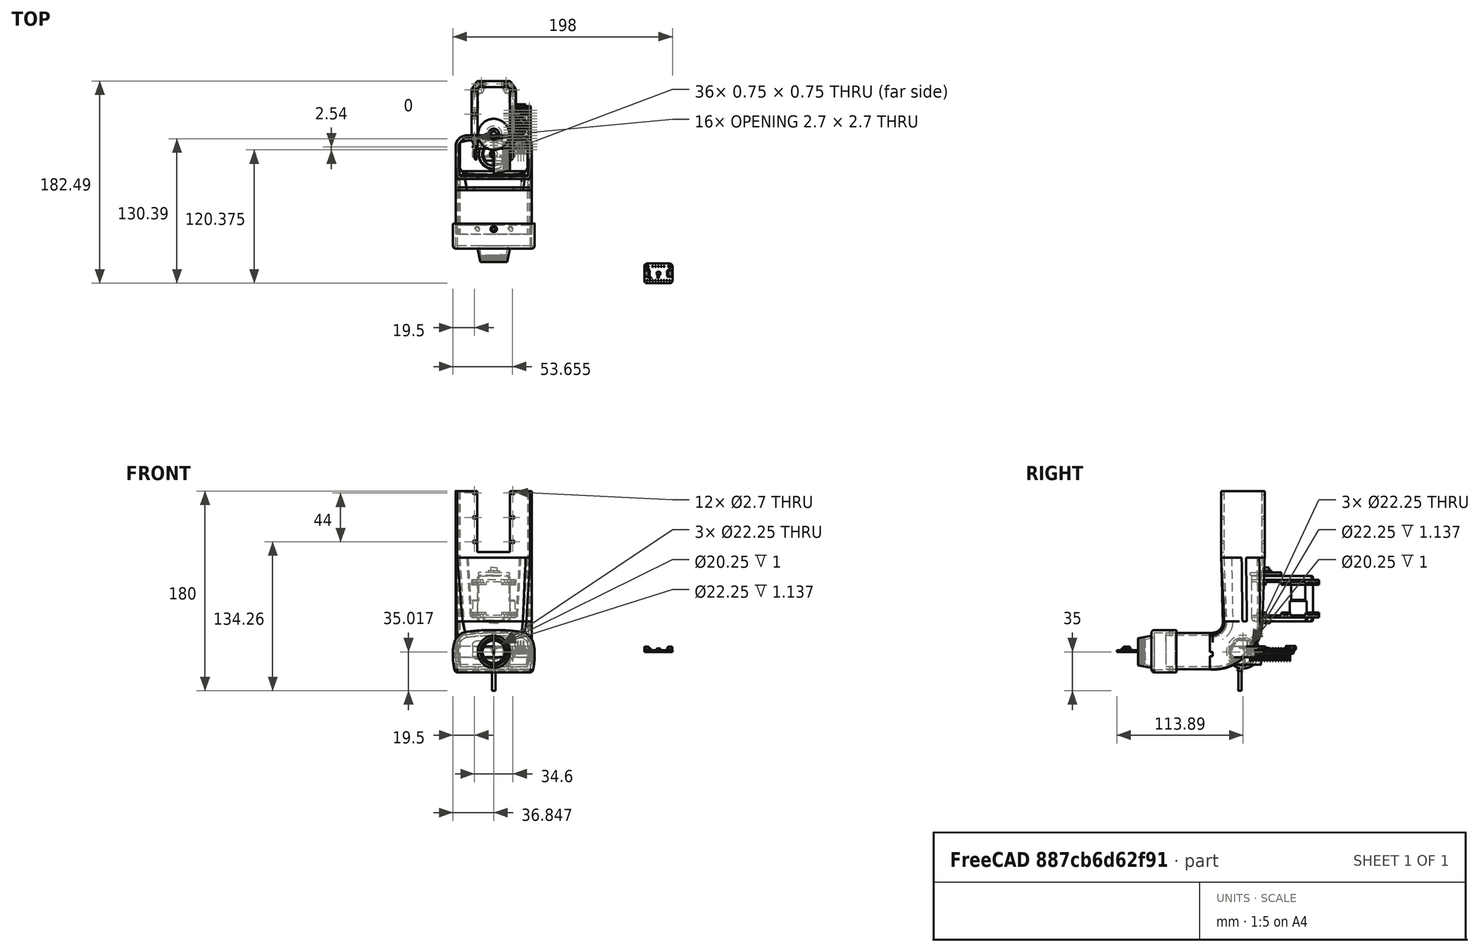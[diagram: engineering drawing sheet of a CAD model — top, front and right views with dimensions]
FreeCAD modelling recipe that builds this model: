
FCSTD DOCUMENT  (FreeCAD 0.20R29177 +426 (Git))
Label: new-mapping-unit 
License: All rights reserved
LicenseURL: http://en.wikipedia.org/wiki/All_rights_reserved
objects: Part::Feature×37, Sketcher::SketchObject×15, PartDesign::Hole×5, PartDesign::Pocket×3, PartDesign::Body×3, App::LinkGroup×2, Spreadsheet::Sheet×2, Part::Compound2×2, Part::Part2DObjectPython×2, PartDesign::AdditiveLoft×2, Mesh::Feature×1, PartDesign::Revolution×1, PartDesign::Pad×1, PartDesign::Thickness×1, PartDesign::SubtractivePipe×1, PartDesign::SubtractiveHelix×1, PartDesign::Boolean×1, PartDesign::AdditivePipe×1
note: 90 computed .brp shape members not serialized (recipe doc carries the construction recipe); baked Part::Feature solids carry a one-line shape summary decoded from their .brp

FEATURE [Part::Feature] Solid  label="DC05_M01_DUMMY"
  Placement = pos=(0,20.5,48) rot=(0,0,1;3.14159rad)
  shape: bbox 40.22 x 62.12 x 50.02 mm, 366 faces (baked)
FEATURE [Mesh::Feature] lidar_mounting_bracket_Body  label="lidar-mounting-bracket-Body"
  Placement = pos=(-0.23,-44.82,76.58) rot=(0.57735,0.57735,0.57735;4.18879rad)
FEATURE [App::LinkGroup] LinkGroup  label="servoLidar"
  ElementList = -> [Solid,lidar_mounting_bracket_Body]
  LinkMode = 0
  Placement = pos=(5.96046e-08,48,82.76) rot=(1,0,0;1.5708rad)
FEATURE [Sketcher::SketchObject] Sketch008
  FullyConstrained = false
  MapMode = 5
  Support = -> [XY_Plane002]
  expr: Constraints[9] = 22.25mm / 2
  sketch-geometry (8):
    g0: LineSegment StartX=9.7 StartY=11.125 StartZ=0 EndX=13.7 EndY=11.125 EndZ=0
    g1: LineSegment StartX=13.7 StartY=11.125 StartZ=0 EndX=13.7 EndY=10.125 EndZ=0
    g2: LineSegment StartX=13.7 StartY=10.125 StartZ=0 EndX=14.7 EndY=10.125 EndZ=0
    g3: LineSegment StartX=14.7 StartY=10.125 StartZ=0 EndX=14.7 EndY=12.1585 EndZ=0
    g4: LineSegment StartX=14.7 StartY=12.1585 StartZ=0 EndX=0 EndY=15 EndZ=0
    g5: LineSegment StartX=0 StartY=15 StartZ=0 EndX=0 EndY=13 EndZ=0
    g6: LineSegment StartX=9.7 StartY=11.125 StartZ=0 EndX=0 EndY=13 EndZ=0
    g7: GeomPoint X=4.20241 Y=12.8749 Z=0
  constraints (21):
    c: Horizontal(g0)
    c: Coincident(g0,g1)
    c: Vertical(g1)
    c: Coincident(g1,g2)
    c: Horizontal(g2)
    c: Coincident(g2,g3)
    c: Vertical(g3)
    c: Coincident(g3,g4)
    c: PointOnObject(g4,g-2)
    c: DistanceY(g-1,g0) = 11.125
    c: DistanceY(g1,g1) = 1
    c: DistanceX(g2,g2) = 1
    c: DistanceX(g0,g0) = 4
    c: DistanceX(g-1,g0) = 13.7
    c: PointOnObject(g5,g-2)
    c: Coincident(g5,g4)
    c: DistanceY(g-1,g4) = 15
    c: Coincident(g6,g0)
    c: Coincident(g6,g5)
    c: Parallel(g6,g4)
    c: DistanceY(g5,g5) = 2
FEATURE [PartDesign::Revolution] Revolution
  Angle = 360
  Axis = (1,0,0)
  Base = (0,0,0)
  Profile = -> Sketch008
  ReferenceAxis = -> Sketch008 [H_Axis]
FEATURE [Sketcher::SketchObject] Sketch009  label="baseSketch"
  FullyConstrained = true
  MapMode = 5
  Placement = pos=(0,0,0) rot=(0.57735,0.57735,0.57735;2.0944rad)
  Support = -> [YZ_Plane003]
  expr: Constraints[14] = <<params>>.cameraWidthBottom
  expr: Constraints[17] = <<params>>.notchWidth
  expr: Constraints[29] = <<params>>.cameraWidth
  expr: Constraints[7] = <<params>>.cameraHeight
  sketch-geometry (12):
    g0: LineSegment StartX=32.85 StartY=-16 StartZ=0 EndX=-32.85 EndY=-16 EndZ=0
    g1: ArcOfCircle CenterX=-22.9627 CenterY=5.1188 CenterZ=0 NormalX=0 NormalY=0 NormalZ=1 AngleXU=0 Radius=10.5 StartAngle=1.72137 EndAngle=2.7983
    g2: ArcOfCircle CenterX=22.9627 CenterY=5.1188 CenterZ=0 NormalX=0 NormalY=0 NormalZ=1 AngleXU=0 Radius=10.5 StartAngle=0.34329 EndAngle=1.42022
    g3: ArcOfCircle CenterX=-2 CenterY=-133.046 CenterZ=0 NormalX=0 NormalY=0 NormalZ=1 AngleXU=0 Radius=150.246 StartAngle=1.5708 EndAngle=1.72137
    g4: ArcOfCircle CenterX=2 CenterY=-133.046 CenterZ=0 NormalX=0 NormalY=0 NormalZ=1 AngleXU=0 Radius=150.246 StartAngle=1.42022 EndAngle=1.5708
    g5: LineSegment StartX=-2 StartY=17.2 StartZ=0 EndX=2 EndY=17.2 EndZ=0
    g6: ArcOfCircle CenterX=-8.64204 CenterY=0 CenterZ=0 NormalX=0 NormalY=0 NormalZ=1 AngleXU=0 Radius=25.708 StartAngle=2.7983 EndAngle=3.14159
    g7: ArcOfCircle CenterX=14.4 CenterY=-4 CenterZ=0 NormalX=0 NormalY=0 NormalZ=1 AngleXU=0 Radius=48.75 StartAngle=3.14159 EndAngle=3.3903
    g8: LineSegment StartX=-34.35 StartY=3.1e-15 StartZ=0 EndX=-34.35 EndY=-4 EndZ=0
    g9: ArcOfCircle CenterX=-14.4 CenterY=-4 CenterZ=0 NormalX=0 NormalY=0 NormalZ=1 AngleXU=0 Radius=48.75 StartAngle=6.03448 EndAngle=6.28319
    g10: ArcOfCircle CenterX=8.64204 CenterY=-9.8e-15 CenterZ=0 NormalX=0 NormalY=0 NormalZ=1 AngleXU=0 Radius=25.708 StartAngle=0 EndAngle=0.34329
    g11: LineSegment StartX=34.35 StartY=-9.8e-15 StartZ=0 EndX=34.35 EndY=-4 EndZ=0
  constraints (32):
    c: Distance(g-1,g0) = 16
    c: Equal(g2,g1)
    c: Symmetric(g0,g0,g-2)
    c: Diameter(g1) = 21
    c: Equal(g4,g3)
    c: Tangent(g4,g2) = -1.5708
    c: Tangent(g3,g1) = -1.5708
    c: Distance(g3,g0) = 33.2
    c: Coincident(g7,g0)
    c: Tangent(g6,g1) = -1.5708
    c: Coincident(g9,g0)
    c: Tangent(g10,g2) = -1.5708
    c: Symmetric(g2,g1,g-2)
    c: Vertical(g1,g0)
    c: DistanceX(g0,g0) = 65.7
    c: Distance(g2,g0) = 31.5
    c: Horizontal(g5)
    c: DistanceX(g5,g5) = 4
    c: Tangent(g5,g4) = 1.5708
    c: Tangent(g5,g3) = 1.5708
    c: Vertical(g8)
    c: Vertical(g11)
    c: Equal(g8,g11)
    c: Equal(g11,g5)
    c: Tangent(g8,g7) = -1.5708
    c: Tangent(g8,g6) = -1.5708
    c: Tangent(g11,g9) = 1.5708
    c: Tangent(g11,g10) = 1.5708
    c: Equal(g9,g7)
    c: DistanceX(g6,g10) = 68.7
    c: PointOnObject(g6,g-1)
    c: Equal(g6,g10)
FEATURE [PartDesign::Pad] Pad003  label="Pad"
  Direction = (1,-2e-16,3e-16)
  Length = 20
  Length2 = 10
  Placement = pos=(0,0,0) rot=(0.57735,0.57735,0.57735;2.0944rad)
  Profile = -> Sketch009
  ReferenceAxis = -> Sketch009 [N_Axis]
  Reversed = true
  Type = 0
  expr: Length = <<params>>.cameraDepth
FEATURE [PartDesign::Thickness] Thickness
  Base = -> Pad003 [Face14]
  BaseFeature = -> Pad003
  Intersection = false
  Join = 0
  Mode = 0
  SupportTransform = false
  Value = 2.5
  expr: Value = <<params>>.wallThickness
FEATURE [Sketcher::SketchObject] Sketch010  label="Sketch002"
  FullyConstrained = true
  MapMode = 5
  Placement = pos=(0,0,0) rot=(0.57735,0.57735,0.57735;2.0944rad)
  Support = -> [YZ_Plane003]
  sketch-geometry (1):
    g0: Circle CenterX=0 CenterY=0 CenterZ=0 NormalX=0 NormalY=0 NormalZ=1 AngleXU=0 Radius=13
  constraints (2):
    c: Coincident(g0,g-1)
    c: Diameter(g0) = 26
FEATURE [PartDesign::Pocket] Pocket004  label="Pocket"
  BaseFeature = -> Thickness
  Direction = (-1,2e-16,-3e-16)
  Length = 5
  Length2 = 5
  Profile = -> Sketch010
  ReferenceAxis = -> Sketch010 [N_Axis]
  Reversed = true
  Type = 1
FEATURE [Spreadsheet::Sheet] Spreadsheet001  label="params"
  cells = A1=cameraWidth; B1(cameraWidth)==68.7mm; D1=wallThickness; E1(wallThickness)==2.5mm; A2=cameraWidthBottom; B2(cameraWidthBottom)==65.7mm; A3=cameraHeight; B3(cameraHeight)==33.2mm; A4=cameraDepth; B4(cameraDepth)==20mm; A5=cameraBottomToSensor; B5(cameraBottomToSensor)==16mm; A7=notchWidth; B7(notchWidth)==4mm
FEATURE [Sketcher::SketchObject] Sketch011  label="grooveSketch"
  FullyConstrained = true
  MapMode = 5
  Placement = pos=(0,0,0) rot=(1,0,0;1.5708rad)
  Support = -> [XZ_Plane003]
  expr: Constraints[6] = <<params>>.wallThickness / 2
  expr: Constraints[7] = <<params>>.cameraBottomToSensor
  expr: Constraints[8] = <<params>>.cameraDepth
  sketch-geometry (3):
    g0: LineSegment StartX=-20 StartY=-17.25 StartZ=0 EndX=-20 EndY=-16 EndZ=0
    g1: LineSegment StartX=-20 StartY=-17.25 StartZ=0 EndX=-18.75 EndY=-16 EndZ=0
    g2: LineSegment StartX=-18.75 StartY=-16 StartZ=0 EndX=-20 EndY=-16 EndZ=0
  constraints (9):
    c: Vertical(g0)
    c: Coincident(g0,g1)
    c: Coincident(g1,g2)
    c: Coincident(g2,g0)
    c: Horizontal(g2)
    c: Equal(g2,g0)
    c: DistanceX(g2,g2) = 1.25
    c: DistanceY(g0,g-1) = 16
    c: DistanceX(g0,g-1) = 20
FEATURE [PartDesign::SubtractivePipe] SubtractivePipe
  AuxilleryCurvelinear = true
  AuxillerySpineTangent = false
  BaseFeature = -> Pocket004
  Binormal = (0,0,0)
  Mode = 0
  Profile = -> Sketch011
  Spine = -> Pocket004 [Edge4,Edge10,Edge21,Edge22,Edge23,Edge24,Edge25,Edge26,Edge27,Edge28,Edge29,Edge7]
  SpineTangent = false
  Transformation = 0
  Transition = 1
FEATURE [Sketcher::SketchObject] Sketch014  label="Sketch006"
  FullyConstrained = true
  MapMode = 5
  Support = -> [XY_Plane002]
  expr: Constraints[7] = 22.25mm / 2 - 0.02mm
  sketch-geometry (3):
    g0: LineSegment StartX=12.951 StartY=-11.105 StartZ=0 EndX=13.3255 EndY=-11.7537 EndZ=0
    g1: LineSegment StartX=13.3255 StartY=-11.7537 StartZ=0 EndX=13.7 EndY=-11.105 EndZ=0
    g2: LineSegment StartX=13.7 StartY=-11.105 StartZ=0 EndX=12.951 EndY=-11.105 EndZ=0
  constraints (9):
    c: Coincident(g0,g1)
    c: Coincident(g1,g2)
    c: Coincident(g2,g0)
    c: Horizontal(g2)
    c: Equal(g1,g2)
    c: Equal(g2,g0)
    c: DistanceX(g2,g2) = 0.749
    c: DistanceY(g1,g-1) = 11.105
    c: DistanceX(g-1,g1) = 13.7
FEATURE [PartDesign::SubtractiveHelix] SubtractiveHelix
  Angle = 0
  Axis = (1,0,0)
  Base = (0,0,0)
  BaseFeature = -> Revolution
  Growth = 0
  HasBeenEdited = true
  Height = 5
  LeftHanded = false
  Mode = 0
  Outside = false
  Pitch = 0.75
  Profile = -> Sketch014
  ReferenceAxis = -> Sketch014 [H_Axis]
  Reversed = true
  Turns = 6.66667
FEATURE [PartDesign::Body] Body002  label="lense"
  Group = -> [Sketch008,Revolution,Sketch014,SubtractiveHelix]
  Origin = -> Origin002
  Tip = -> SubtractiveHelix
FEATURE [PartDesign::Boolean] Boolean002
  BaseFeature = -> SubtractivePipe
  Group = -> [Body002]
  Type = 0
FEATURE [Part::Feature] Feature  label="arduino nano001"
  Placement = pos=(32.0955,6.48515,2e-15) rot=(0.57735,0.57735,0.57735;2.0944rad)
  shape: bbox 18 x 45 x 18.6 mm, 6295 faces, 55 solids (baked)
FEATURE [Part::Feature] Solid002
  shape: bbox 68.8 x 33.82 x 71.73 mm, 134 faces (baked)
FEATURE [Part::Compound2] Compound  label="camera"
  Links = -> [Solid002]
  Placement = pos=(0,-74.85,-2.65) rot=(-1,0,0;4.71239rad)
FEATURE [Part::Feature] Solid003
  shape: bbox 2 x 1.25 x 1.25 mm, 28 faces (baked)
FEATURE [Part::Feature] Solid004
  shape: bbox 1.25 x 2 x 1.25 mm, 28 faces (baked)
FEATURE [Part::Feature] Solid005
  shape: bbox 1.5 x 0.2 x 1.25 mm, 25 faces (baked)
FEATURE [Part::Feature] Solid006
  shape: bbox 3.7 x 0.2 x 2.46 mm, 20 faces (baked)
FEATURE [Part::Feature] Solid007
  shape: bbox 3.7 x 0.2 x 2.46 mm, 20 faces (baked)
FEATURE [Part::Feature] Solid008
  shape: bbox 3.7 x 0.2 x 2.46 mm, 20 faces (baked)
FEATURE [Part::Feature] Solid009
  shape: bbox 1.5 x 0.2 x 1.25 mm, 25 faces (baked)
FEATURE [Part::Feature] Solid010
  shape: bbox 3.7 x 0.2 x 2.46 mm, 20 faces (baked)
FEATURE [Part::Feature] Solid011
  shape: bbox 4.25 x 6 x 2.9 mm, 99 faces (baked)
FEATURE [Part::Feature] Solid012
  shape: bbox 1.5 x 0.2 x 1.25 mm, 25 faces (baked)
FEATURE [Part::Feature] Solid013
  shape: bbox 3.7 x 0.2 x 2.46 mm, 20 faces (baked)
FEATURE [Part::Feature] Solid014
  shape: bbox 3.7 x 0.2 x 2.46 mm, 20 faces (baked)
FEATURE [Part::Feature] Solid015
  shape: bbox 3.7 x 0.2 x 2.46 mm, 20 faces (baked)
FEATURE [Part::Feature] Solid016
  shape: bbox 1.5 x 0.2 x 1.25 mm, 25 faces (baked)
FEATURE [Part::Feature] Solid017
  shape: bbox 3.7 x 0.2 x 2.46 mm, 20 faces (baked)
FEATURE [Part::Feature] Solid018
  shape: bbox 4.25 x 6 x 2.9 mm, 99 faces (baked)
FEATURE [Part::Feature] Solid019
  shape: bbox 1.6 x 0.8 x 1.1 mm, 50 faces (baked)
FEATURE [Part::Feature] Solid020
  shape: bbox 0.1295 x 0.1295 x 0.003 mm, 4 faces (baked)
FEATURE [Part::Feature] Solid021
  shape: bbox 3.098 x 2.59 x 1.346 mm, 6 faces (baked)
FEATURE [Part::Feature] Solid022
  shape: bbox 0.534 x 0.305 x 0.051 mm, 6 faces (baked)
FEATURE [Part::Feature] Solid023
  shape: bbox 0.534 x 0.304 x 0.051 mm, 6 faces (baked)
FEATURE [Part::Feature] Solid024
  shape: bbox 0.534 x 0.304 x 0.051 mm, 6 faces (baked)
FEATURE [Part::Feature] Solid025
  shape: bbox 0.534 x 0.305 x 0.051 mm, 6 faces (baked)
FEATURE [Part::Feature] Solid026
  shape: bbox 0.305 x 0.533 x 0.051 mm, 6 faces (baked)
FEATURE [Part::Feature] Solid027
  shape: bbox 0.304 x 0.533 x 0.051 mm, 6 faces (baked)
FEATURE [Part::Feature] Solid028
  shape: bbox 0.305 x 0.533 x 0.051 mm, 6 faces (baked)
FEATURE [Part::Feature] Solid029
  shape: bbox 0.534 x 0.305 x 0.051 mm, 6 faces (baked)
FEATURE [Part::Feature] Solid030
  shape: bbox 0.534 x 0.304 x 0.051 mm, 6 faces (baked)
FEATURE [Part::Feature] Solid031
  shape: bbox 0.534 x 0.304 x 0.051 mm, 6 faces (baked)
FEATURE [Part::Feature] Solid032
  shape: bbox 0.534 x 0.305 x 0.051 mm, 6 faces (baked)
FEATURE [Part::Feature] Solid033
  shape: bbox 0.305 x 0.533 x 0.051 mm, 6 faces (baked)
FEATURE [Part::Feature] Solid034
  shape: bbox 0.304 x 0.533 x 0.051 mm, 6 faces (baked)
FEATURE [Part::Feature] Solid035
  shape: bbox 0.305 x 0.533 x 0.051 mm, 6 faces (baked)
FEATURE [Part::Feature] Solid036
  shape: bbox 25.4 x 17.78 x 1.68 mm, 42 faces (baked)
FEATURE [Part::Compound2] Compound001  label="Adafruit_ISM330DHXC"
  Links = -> [Solid003,Solid004,Solid005,Solid006,Solid007,Solid008,Solid009,Solid010,Solid011,Solid012,Solid013,Solid014,Solid015,Solid016,Solid017,Solid018,Solid019,Solid020,Solid021,Solid022,Solid023,Solid024,Solid025,Solid026,Solid027,Solid028,Solid029,Solid030,Solid031,Solid032,Solid033,Solid034,Solid035,Solid036]
  Placement = pos=(104.659,174.995,0) rot=(0,0,1;4.71239rad)
FEATURE [App::LinkGroup] LinkGroup001  label="nanoIMU"
  ElementList = -> [Feature,Compound001]
  LinkMode = 0
  Placement = pos=(-12,-57.5,-5.96046e-08) rot=(0,0,1;0rad)
FEATURE [Sketcher::SketchObject] Sketch015  label="horizontalPipe"
  AttachmentOffset = pos=(0,0,30) rot=(0,0,1;0rad)
  FullyConstrained = true
  MapMode = 5
  Placement = pos=(0,-30,-6.7e-15) rot=(1,0,0;1.5708rad)
  Support = -> [XZ_Plane008]
  expr: Constraints[12] = <<Parameter>>.horizontalWidthBottom
  expr: Constraints[14] = <<Parameter>>.notchWidth
  expr: Constraints[26] = <<Parameter>>.horizontalWidth
  expr: Constraints[2] = <<Parameter>>.horizontalCornerDiameter
  expr: Constraints[32] = <<Parameter>>.notchWidth
  expr: Constraints[33] = <<Parameter>>.horizontalBottomToSensor
  expr: Constraints[34] = <<Parameter>>.horizontalSideHeight
  expr: Constraints[35] = <<Parameter>>.horizontalHeight
  expr: Constraints[41] = <<Parameter>>.horizontalWidthBottom - <<Parameter>>.wallThickness * 2
  expr: Constraints[42] = <<Parameter>>.horizontalBottomToSensor - <<Parameter>>.wallThickness
  expr: Constraints[43] = <<Parameter>>.horizontalHeight - <<Parameter>>.wallThickness * 2
  expr: Constraints[44] = <<Parameter>>.horizontalWidth - <<Parameter>>.wallThickness * 2
  expr: Constraints[57] = <<Parameter>>.horizontalCornerDiameter - <<Parameter>>.wallThickness * 2
  expr: Constraints[63] = <<Parameter>>.horizontalSideHeight - <<Parameter>>.wallThickness * 2
  sketch-geometry (24):
    g0: LineSegment StartX=32.75 StartY=-15.8 StartZ=0 EndX=-32.75 EndY=-15.8 EndZ=0
    g1: ArcOfCircle CenterX=-22.8638 CenterY=5.10699 CenterZ=0 NormalX=0 NormalY=0 NormalZ=1 AngleXU=0 Radius=10.5 StartAngle=1.71367 EndAngle=2.79797
    g2: ArcOfCircle CenterX=22.8638 CenterY=5.10699 CenterZ=0 NormalX=0 NormalY=0 NormalZ=1 AngleXU=0 Radius=10.5 StartAngle=0.343622 EndAngle=1.42792
    g3: ArcOfCircle CenterX=-2 CenterY=-139.925 CenterZ=0 NormalX=0 NormalY=0 NormalZ=1 AngleXU=0 Radius=157.025 StartAngle=1.5708 EndAngle=1.71367
    g4: ArcOfCircle CenterX=2 CenterY=-139.925 CenterZ=0 NormalX=0 NormalY=0 NormalZ=1 AngleXU=0 Radius=157.025 StartAngle=1.42792 EndAngle=1.5708
    g5: LineSegment StartX=-2 StartY=17.1 StartZ=0 EndX=2 EndY=17.1 EndZ=0
    g6: ArcOfCircle CenterX=-8.59123 CenterY=0 CenterZ=0 NormalX=0 NormalY=0 NormalZ=1 AngleXU=0 Radius=25.6588 StartAngle=2.79797 EndAngle=3.14159
    g7: ArcOfCircle CenterX=12.9133 CenterY=-4 CenterZ=0 NormalX=0 NormalY=0 NormalZ=1 AngleXU=0 Radius=47.1633 StartAngle=3.14159 EndAngle=3.39447
    g8: LineSegment StartX=-34.25 StartY=3.1e-15 StartZ=0 EndX=-34.25 EndY=-4 EndZ=0
    g9: ArcOfCircle CenterX=-12.9133 CenterY=-4 CenterZ=0 NormalX=0 NormalY=0 NormalZ=1 AngleXU=0 Radius=47.1633 StartAngle=6.0303 EndAngle=6.28319
    g10: ArcOfCircle CenterX=8.59123 CenterY=9.6e-15 CenterZ=0 NormalX=0 NormalY=0 NormalZ=1 AngleXU=0 Radius=25.6588 StartAngle=0 EndAngle=0.343622
    g11: LineSegment StartX=34.25 StartY=9.6e-15 StartZ=0 EndX=34.25 EndY=-4 EndZ=0
    g12: LineSegment StartX=-30.35 StartY=-13.4 StartZ=0 EndX=30.35 EndY=-13.4 EndZ=0
    g13: LineSegment StartX=31.85 StartY=-5e-16 StartZ=0 EndX=31.85 EndY=-4 EndZ=0
    g14: LineSegment StartX=-2 StartY=14.7 StartZ=0 EndX=2 EndY=14.7 EndZ=0
    g15: LineSegment StartX=-31.85 StartY=2.7e-15 StartZ=0 EndX=-31.85 EndY=-4 EndZ=0
    g16: ArcOfCircle CenterX=-2 CenterY=-136.961 CenterZ=0 NormalX=0 NormalY=0 NormalZ=1 AngleXU=0 Radius=151.661 StartAngle=1.5708 EndAngle=1.71618
    g17: ArcOfCircle CenterX=-22.7982 CenterY=5.08545 CenterZ=0 NormalX=0 NormalY=0 NormalZ=1 AngleXU=0 Radius=8.1 StartAngle=1.71618 EndAngle=2.77156
    g18: ArcOfCircle CenterX=-9.68789 CenterY=0 CenterZ=0 NormalX=0 NormalY=0 NormalZ=1 AngleXU=0 Radius=22.1621 StartAngle=2.77156 EndAngle=3.14159
    g19: ArcOfCircle CenterX=-1.64667 CenterY=-4 CenterZ=0 NormalX=0 NormalY=0 NormalZ=1 AngleXU=0 Radius=30.2033 StartAngle=3.14159 EndAngle=3.45807
    g20: ArcOfCircle CenterX=1.64667 CenterY=-4 CenterZ=0 NormalX=0 NormalY=0 NormalZ=1 AngleXU=0 Radius=30.2033 StartAngle=5.9667 EndAngle=6.28319
    g21: ArcOfCircle CenterX=2 CenterY=-136.961 CenterZ=0 NormalX=0 NormalY=0 NormalZ=1 AngleXU=0 Radius=151.661 StartAngle=1.42541 EndAngle=1.5708
    g22: ArcOfCircle CenterX=22.7982 CenterY=5.08545 CenterZ=0 NormalX=0 NormalY=0 NormalZ=1 AngleXU=0 Radius=8.1 StartAngle=0.370029 EndAngle=1.42541
    g23: ArcOfCircle CenterX=9.68789 CenterY=-2.7e-15 CenterZ=0 NormalX=0 NormalY=0 NormalZ=1 AngleXU=0 Radius=22.1621 StartAngle=1e-16 EndAngle=0.370029
  constraints (64):
    c: Equal(g2,g1)
    c: Symmetric(g0,g0,g-2)
    c: Diameter(g1) = 21
    c: Equal(g4,g3)
    c: Tangent(g4,g2) = -1.5708
    c: Tangent(g3,g1) = -1.5708
    c: Coincident(g7,g0)
    c: Tangent(g6,g1) = -1.5708
    c: Coincident(g9,g0)
    c: Tangent(g10,g2) = -1.5708
    c: Symmetric(g2,g1,g-2)
    c: Vertical(g1,g0)
    c: DistanceX(g0,g0) = 65.5
    c: Horizontal(g5)
    c: DistanceX(g5,g5) = 4
    c: Tangent(g5,g4) = 1.5708
    c: Tangent(g5,g3) = 1.5708
    c: Vertical(g8)
    c: Vertical(g11)
    c: Equal(g8,g11)
    c: Equal(g11,g5)
    c: Tangent(g8,g7) = -1.5708
    c: Tangent(g8,g6) = -1.5708
    c: Tangent(g11,g9) = 1.5708
    c: Tangent(g11,g10) = 1.5708
    c: Equal(g9,g7)
    c: DistanceX(g6,g10) = 68.5
    c: PointOnObject(g6,g-1)
    c: Equal(g6,g10)
    c: Symmetric(g12,g12,g-2)
    c: Vertical(g13)
    c: Symmetric(g14,g14,g-2)
    c: DistanceX(g14,g14) = 4
    c: Distance(g-1,g0) = 15.8
    c: Distance(g2,g0) = 31.3
    c: Distance(g4,g0) = 32.9
    c: PointOnObject(g13,g-1)
    c: PointOnObject(g15,g-1)
    c: Vertical(g15)
    c: Equal(g15,g13)
    c: Equal(g13,g14)
    c: DistanceX(g12,g12) = 60.7
    c: Distance(g-1,g12) = 13.4
    c: Distance(g14,g12) = 28.1
    c: DistanceX(g15,g13) = 63.7
    c: Coincident(g19,g12)
    c: Coincident(g20,g12)
    c: Tangent(g17,g16) = -1.5708
    c: Tangent(g16,g14) = 1.5708
    c: Tangent(g14,g21) = 1.5708
    c: Tangent(g21,g22) = -1.5708
    c: Tangent(g22,g23) = -1.5708
    c: Tangent(g23,g13) = 1.5708
    c: Tangent(g13,g20) = 1.5708
    c: Tangent(g15,g19) = -1.5708
    c: Tangent(g18,g17) = -1.5708
    c: Tangent(g15,g18) = -1.5708
    c: Diameter(g17) = 16.2
    c: Vertical(g12,g17)
    c: Vertical(g12,g22)
    c: Equal(g22,g17)
    c: Equal(g16,g21)
    c: Equal(g19,g20)
    c: Distance(g21,g12) = 26.5
FEATURE [Sketcher::SketchObject] Sketch017
  FullyConstrained = true
  MapMode = 5
  Placement = pos=(0,0,0) rot=(0.57735,0.57735,0.57735;2.0944rad)
  Support = -> [YZ_Plane008]
  expr: Constraints[11] = <<Parameter>>.horizontalDepth
  expr: Constraints[8] = <<Parameter>>.verticalHeight
  sketch-geometry (7):
    g0: LineSegment StartX=0 StartY=85 StartZ=0 EndX=0 EndY=27.5 EndZ=0
    g1: LineSegment StartX=-30 StartY=0 StartZ=0 EndX=-27.5 EndY=0 EndZ=0
    g2: LineSegment StartX=0 StartY=0 StartZ=0 EndX=0 EndY=145 EndZ=0
    g3: LineSegment StartX=0 StartY=0 StartZ=0 EndX=-69.5 EndY=0 EndZ=0
    g4: ArcOfCircle CenterX=-27.5 CenterY=27.5 CenterZ=0 NormalX=0 NormalY=0 NormalZ=1 AngleXU=0 Radius=27.5 StartAngle=5.85787 EndAngle=6.28319
    g5: ArcOfCircle CenterX=-27.5 CenterY=27.5 CenterZ=0 NormalX=0 NormalY=0 NormalZ=1 AngleXU=0 Radius=27.5 StartAngle=4.71239 EndAngle=5.20106
    g6: ArcOfCircle CenterX=-27.5 CenterY=27.5 CenterZ=0 NormalX=0 NormalY=0 NormalZ=1 AngleXU=0 Radius=27.5 StartAngle=5.20106 EndAngle=5.85787
  constraints (21):
    c: PointOnObject(g0,g-2)
    c: PointOnObject(g1,g-1)
    c: PointOnObject(g1,g-1)
    c: Vertical(g0)
    c: Tangent(g1,g5) = -1.5708
    c: Tangent(g0,g4) = 1.5708
    c: Coincident(g2,g-1)
    c: PointOnObject(g2,g-2)
    c: DistanceY(g2,g2) = 145
    c: Coincident(g3,g2)
    c: PointOnObject(g3,g-1)
    c: DistanceX(g3,g3) = 69.5
    c: DistanceY(g0,g2) = 60
    c: DistanceX(g1,g2) = 30
    c: Coincident(g6,g4)
    c: Coincident(g5,g4)
    c: Coincident(g5,g6)
    c: Coincident(g5,g6)
    c: Diameter(g5) = 55
    c: DistanceX(g4,g2) = 2.45
    c: DistanceX(g5,g2) = 14.59
FEATURE [Sketcher::SketchObject] Sketch018  label="verticalPipe"
  AttachmentOffset = pos=(0,0,85) rot=(0,0,1;0rad)
  FullyConstrained = true
  MapMode = 5
  Placement = pos=(0,0,85) rot=(0,0,1;0rad)
  Support = -> [XY_Plane008]
  expr: Constraints[15] = <<Parameter>>.verticalLength + <<Parameter>>.threshold
  expr: Constraints[1] = <<Parameter>>.vertialWidthTop
  expr: Constraints[24] = <<Parameter>>.vertialWidthTop - <<Parameter>>.wallThickness * 2
  expr: Constraints[25] = <<Parameter>>.vertialWidthBottom - <<Parameter>>.wallThickness
  expr: Constraints[26] = <<Parameter>>.verticalLength - <<Parameter>>.wallThickness * 2 + <<Parameter>>.threshold
  expr: Constraints[40] = <<Parameter>>.verticalLength / 2
  sketch-geometry (16):
    g0: LineSegment StartX=-32.85 StartY=-19.7 StartZ=0 EndX=32.85 EndY=-19.7 EndZ=0
    g1: LineSegment StartX=-24.35 StartY=19.5 StartZ=0 EndX=24.35 EndY=19.5 EndZ=0
    g2: LineSegment StartX=-34.35 StartY=9.5 StartZ=0 EndX=-34.35 EndY=-4 EndZ=0
    g3: LineSegment StartX=34.35 StartY=9.5 StartZ=0 EndX=34.35 EndY=-4 EndZ=0
    g4: ArcOfCircle CenterX=-24.35 CenterY=9.5 CenterZ=0 NormalX=0 NormalY=0 NormalZ=1 AngleXU=0 Radius=10 StartAngle=1.5708 EndAngle=3.14159
    g5: ArcOfCircle CenterX=48.5633 CenterY=-4 CenterZ=0 NormalX=0 NormalY=0 NormalZ=1 AngleXU=0 Radius=82.9133 StartAngle=3.14159 EndAngle=3.3321
    g6: ArcOfCircle CenterX=-48.5633 CenterY=-4 CenterZ=0 NormalX=0 NormalY=0 NormalZ=1 AngleXU=0 Radius=82.9133 StartAngle=6.09268 EndAngle=6.28319
    g7: ArcOfCircle CenterX=24.35 CenterY=9.5 CenterZ=0 NormalX=0 NormalY=0 NormalZ=1 AngleXU=0 Radius=10 StartAngle=2e-16 EndAngle=1.5708
    g8: LineSegment StartX=-30.45 StartY=-17.3 StartZ=0 EndX=30.45 EndY=-17.3 EndZ=0
    g9: LineSegment StartX=-23.15 StartY=17.1 StartZ=0 EndX=23.15 EndY=17.1 EndZ=0
    g10: LineSegment StartX=31.5 StartY=8.75 StartZ=0 EndX=31.5 EndY=-4.75 EndZ=0
    g11: LineSegment StartX=-31.5 StartY=8.75 StartZ=0 EndX=-31.5 EndY=-4.75 EndZ=0
    g12: ArcOfCircle CenterX=-23.15 CenterY=8.75 CenterZ=0 NormalX=0 NormalY=0 NormalZ=1 AngleXU=0 Radius=8.35 StartAngle=1.5708 EndAngle=3.14159
    g13: ArcOfCircle CenterX=44.0262 CenterY=-4.75 CenterZ=0 NormalX=0 NormalY=0 NormalZ=1 AngleXU=0 Radius=75.5262 StartAngle=3.14159 EndAngle=3.30853
    g14: ArcOfCircle CenterX=23.15 CenterY=8.75 CenterZ=0 NormalX=0 NormalY=0 NormalZ=1 AngleXU=0 Radius=8.35 StartAngle=1e-16 EndAngle=1.5708
    g15: ArcOfCircle CenterX=-44.0262 CenterY=-4.75 CenterZ=0 NormalX=0 NormalY=0 NormalZ=1 AngleXU=0 Radius=75.5262 StartAngle=6.11624 EndAngle=6.28319
  constraints (41):
    c: Horizontal(g1)
    c: DistanceX(g0,g0) = 65.7
    c: Vertical(g3)
    c: Horizontal(g2,g3)
    c: Equal(g2,g3)
    c: Coincident(g6,g0)
    c: Coincident(g5,g0)
    c: Tangent(g4,g1) = 1.5708
    c: Tangent(g4,g2) = -1.5708
    c: Tangent(g5,g2) = -1.5708
    c: Tangent(g3,g6) = 1.5708
    c: Tangent(g7,g3) = 1.5708
    c: Tangent(g1,g7) = 1.5708
    c: Equal(g5,g6)
    c: Diameter(g4) = 20
    c: Distance(g1,g0) = 39.2
    c: DistanceX(g1,g1) = 48.7
    c: Symmetric(g0,g0,g-2)
    c: Vertical(g10)
    c: Symmetric(g9,g9,g-2)
    c: Symmetric(g8,g8,g-2)
    c: Horizontal(g10,g11)
    c: Equal(g10,g11)
    c: DistanceY(g11,g11) = 13.5
    c: DistanceX(g8,g8) = 60.9
    c: DistanceX(g9,g9) = 46.3
    c: Distance(g9,g8) = 34.4
    c: Tangent(g10,g15) = 1.5708
    c: Tangent(g14,g10) = 1.5708
    c: Tangent(g14,g9) = 1.5708
    c: Tangent(g9,g12) = 1.5708
    c: Tangent(g12,g11) = -1.5708
    c: Tangent(g13,g11) = -1.5708
    c: Coincident(g8,g13)
    c: Coincident(g8,g15)
    c: Vertical(g11)
    c: DistanceY(g2,g2) = 13.5
    c: DistanceX(g11,g10) = 63
    c: Distance(g9,g1) = 2.4
    c: Vertical(g2)
    c: Distance(g-1,g1) = 19.5
FEATURE [Spreadsheet::Sheet] Spreadsheet002  label="Parameter"
  cells = A1=vertialWidthTop; B1(vertialWidthTop)==65.7mm; A2=verticalLength; B2(verticalLength)==39mm; A3=vertialWidthBottom; B3(vertialWidthBottom)==48.7mm; A4=cornnerDiameter; B4(cornnerDiameter)==21mm; A5=wallThickness; B5(wallThickness)==2.4mm; A6=verticalHeight; B6(verticalHeight)==145mm; D7=threshold; E7(threshold)==0.2mm; A9=horizontalWidth; B9(horizontalWidth)==68.7mm - E7; A10=horizontalWidthBottom; B10(horizontalWidthBottom)==65.7mm - E7; A11=horizontalHeight; B11(horizontalHeight)==33.2mm - 1.5 * E7; A12=notchWidth; B12(notchWidth)==4mm; A13=horizontalCornerDiameter; B13(horizontalCornerDiameter)==21mm; A14=horizontalDepth; B14(horizontalDepth)==69.5mm; A15=horizontalBottomToSensor; B15(horizontalBottomToSensor)==16mm - E7; A16=horizontalSideHeight; B16(horizontalSideHeight)==31.5mm - E7; A20=servoScrewHoleWidth; B20(servoScrewHoleWidth)==34.6mm; A21=servoScrewHoleLength; B21(servoScrewHoleLength)==45.74mm; A22=servoScewHoleDiameter; B22(servoScewHoleDiameter)==2.7mm
FEATURE [Sketcher::SketchObject] Sketch  label="sevoCutout"
  FullyConstrained = true
  MapMode = 5
  Placement = pos=(0,0,0) rot=(1,0,0;1.5708rad)
  Support = -> [XZ_Plane008]
  expr: Constraints[9] = <<Parameter>>.verticalHeight
  sketch-geometry (4):
    g0: LineSegment StartX=-14.75 StartY=145 StartZ=0 EndX=14.75 EndY=145 EndZ=0
    g1: LineSegment StartX=14.75 StartY=145 StartZ=0 EndX=14.75 EndY=90 EndZ=0
    g2: LineSegment StartX=14.75 StartY=90 StartZ=0 EndX=-14.75 EndY=90 EndZ=0
    g3: LineSegment StartX=-14.75 StartY=90 StartZ=0 EndX=-14.75 EndY=145 EndZ=0
  constraints (11):
    c: Coincident(g0,g1)
    c: Coincident(g1,g2)
    c: Coincident(g2,g3)
    c: Coincident(g3,g0)
    c: Horizontal(g2)
    c: Vertical(g1)
    c: Vertical(g3)
    c: Symmetric(g0,g0,g-2)
    c: DistanceX(g0,g0) = 29.5
    c: Distance(g-1,g0) = 145
    c: DistanceY(g1,g1) = 55
FEATURE [Sketcher::SketchObject] Sketch019  label="servoScrewHole"
  AttachmentOffset = pos=(0,0,21) rot=(0,0,1;0rad)
  FullyConstrained = true
  MapMode = 5
  Placement = pos=(0,-21,-4.7e-15) rot=(1,0,0;1.5708rad)
  Support = -> [XZ_Plane008]
  expr: Constraints[21] = <<Parameter>>.servoScewHoleDiameter
  expr: Constraints[22] = <<Parameter>>.servoScrewHoleLength
  expr: Constraints[8] = Spreadsheet002.servoScrewHoleWidth
  expr: Constraints[9] = <<Parameter>>.verticalHeight
  sketch-geometry (10):
    g0: LineSegment StartX=-17.3 StartY=145 StartZ=0 EndX=17.3 EndY=145 EndZ=0
    g1: LineSegment StartX=17.3 StartY=145 StartZ=0 EndX=17.3 EndY=99.26 EndZ=0
    g2: LineSegment StartX=17.3 StartY=99.26 StartZ=0 EndX=-17.3 EndY=99.26 EndZ=0
    g3: LineSegment StartX=-17.3 StartY=99.26 StartZ=0 EndX=-17.3 EndY=145 EndZ=0
    g4: Circle CenterX=-17.3 CenterY=143.26 CenterZ=0 NormalX=0 NormalY=0 NormalZ=1 AngleXU=0 Radius=1.35
    g5: Circle CenterX=-17.3 CenterY=121.26 CenterZ=0 NormalX=0 NormalY=0 NormalZ=1 AngleXU=0 Radius=1.35
    g6: Circle CenterX=17.3 CenterY=143.26 CenterZ=0 NormalX=0 NormalY=0 NormalZ=1 AngleXU=0 Radius=1.35
    g7: Circle CenterX=17.3 CenterY=121.26 CenterZ=0 NormalX=0 NormalY=0 NormalZ=1 AngleXU=0 Radius=1.35
    g8: Circle CenterX=17.3 CenterY=99.26 CenterZ=0 NormalX=0 NormalY=0 NormalZ=1 AngleXU=0 Radius=1.35
    g9: Circle CenterX=-17.3 CenterY=99.26 CenterZ=0 NormalX=0 NormalY=0 NormalZ=1 AngleXU=0 Radius=1.35
  constraints (27):
    c: Coincident(g0,g1)
    c: Coincident(g1,g2)
    c: Coincident(g2,g3)
    c: Coincident(g3,g0)
    c: Horizontal(g2)
    c: Vertical(g1)
    c: Vertical(g3)
    c: Symmetric(g0,g0,g-2)
    c: DistanceX(g0,g0) = 34.6
    c: Distance(g-1,g0) = 145
    c: PointOnObject(g4,g3)
    c: PointOnObject(g5,g3)
    c: PointOnObject(g6,g1)
    c: PointOnObject(g7,g1)
    c: Coincident(g8,g1)
    c: Coincident(g9,g2)
    c: Equal(g9,g8)
    c: Equal(g8,g7)
    c: Equal(g7,g5)
    c: Equal(g5,g4)
    c: Equal(g4,g6)
    c: Diameter(g4) = 2.7
    c: DistanceY(g3,g3) = 45.74
    c: Horizontal(g5,g7)
    c: Horizontal(g4,g6)
    c: DistanceY(g8,g7) = 22
    c: DistanceY(g7,g6) = 22
FEATURE [Sketcher::SketchObject] Sketch020  label="cableRoute"
  FullyConstrained = true
  MapMode = 5
  Placement = pos=(0,0,0) rot=(1,0,0;1.5708rad)
  Support = -> [XZ_Plane008]
  sketch-geometry (10):
    g0: ArcOfCircle CenterX=-15 CenterY=5.79 CenterZ=0 NormalX=0 NormalY=0 NormalZ=1 AngleXU=0 Radius=4.13 StartAngle=1.5708 EndAngle=3.14159
    g1: LineSegment StartX=-15 StartY=9.92 StartZ=0 EndX=15 EndY=9.92 EndZ=0
    g2: ArcOfCircle CenterX=15 CenterY=5.79 CenterZ=0 NormalX=0 NormalY=0 NormalZ=1 AngleXU=0 Radius=4.13 StartAngle=2e-16 EndAngle=1.5708
    g3: LineSegment StartX=19.13 StartY=5.79 StartZ=0 EndX=19.13 EndY=-2.39 EndZ=0
    g4: ArcOfCircle CenterX=15 CenterY=-2.39 CenterZ=0 NormalX=0 NormalY=0 NormalZ=1 AngleXU=0 Radius=4.13 StartAngle=4.71239 EndAngle=6.28319
    g5: LineSegment StartX=15 StartY=-6.52 StartZ=0 EndX=-15 EndY=-6.52 EndZ=0
    g6: ArcOfCircle CenterX=-15 CenterY=-2.39 CenterZ=0 NormalX=0 NormalY=0 NormalZ=1 AngleXU=0 Radius=4.13 StartAngle=3.14159 EndAngle=4.71239
    g7: LineSegment StartX=-19.13 StartY=-2.39 StartZ=0 EndX=-19.13 EndY=5.79 EndZ=0
    g8: GeomPoint X=-19.13 Y=9.92 Z=0
    g9: GeomPoint X=19.13 Y=-6.52 Z=0
  constraints (23):
    c: Tangent(g0,g1) = 1.5708
    c: Tangent(g1,g2) = 1.5708
    c: Tangent(g2,g3) = 1.5708
    c: Tangent(g3,g4) = 1.5708
    c: Tangent(g4,g5) = 1.5708
    c: Tangent(g5,g6) = 1.5708
    c: Tangent(g6,g7) = 1.5708
    c: Tangent(g7,g0) = 1.5708
    c: Horizontal(g1)
    c: Vertical(g3)
    c: Vertical(g7)
    c: Equal(g0,g2)
    c: Equal(g2,g4)
    c: Equal(g4,g6)
    c: PointOnObject(g8,g1)
    c: PointOnObject(g8,g7)
    c: PointOnObject(g9,g3)
    c: PointOnObject(g9,g5)
    c: Symmetric(g5,g4,g-2)
    c: DistanceX(g1,g1) = 30
    c: DistanceY(g3,g3) = 8.18
    c: Diameter(g6) = 8.26
    c: Distance(g-1,g5) = 6.52
FEATURE [Sketcher::SketchObject] Sketch021  label="scewHoleBottom"
  AttachmentOffset = pos=(0,0,-19) rot=(0,0,1;0rad)
  ExternalGeometry = -> [Boolean002]
  FullyConstrained = true
  MapMode = 5
  Placement = pos=(0,0,-19) rot=(0,0,1;0rad)
  Support = -> [XY_Plane003]
  sketch-geometry (2):
    g0: Circle CenterX=-15 CenterY=-15 CenterZ=0 NormalX=0 NormalY=0 NormalZ=1 AngleXU=0 Radius=1.5
    g1: Circle CenterX=-15 CenterY=15 CenterZ=0 NormalX=0 NormalY=0 NormalZ=1 AngleXU=0 Radius=1.5
  constraints (5):
    c: Equal(g1,g0)
    c: Diameter(g0) = 3
    c: DistanceY(g0,g1) = 30
    c: Symmetric(g0,g1,g-1)
    c: Distance(g1,g-3) = 5
FEATURE [PartDesign::Hole] Hole001  label="scewHoleBottom001"
  BaseFeature = -> Boolean002
  CustomThreadClearance = 0
  Depth = 25
  DepthType = 0
  Diameter = 3
  DrillForDepth = false
  DrillPoint = 1
  DrillPointAngle = 118
  HoleCutCountersinkAngle = 112
  HoleCutCustomValues = false
  HoleCutDepth = 0
  HoleCutDiameter = 6.1
  HoleCutType = 2
  ModelThread = false
  Profile = -> Sketch021
  Reversed = true
  Tapered = false
  TaperedAngle = 90
  ThreadClass = 0
  ThreadDepth = 25
  ThreadDepthType = 0
  ThreadDirection = 0
  ThreadFit = 0
  ThreadSize = 0
  ThreadType = 0
  Threaded = false
  UseCustomThreadClearance = false
FEATURE [Sketcher::SketchObject] Sketch022  label="cameraBottomScrewHole001"
  AttachmentOffset = pos=(0,-4.7,-19) rot=(0,0,1;0rad)
  FullyConstrained = true
  MapMode = 5
  Placement = pos=(0,-4.7,-19) rot=(0,0,1;0rad)
  Support = -> [XY_Plane008]
  sketch-geometry (2):
    g0: Circle CenterX=15 CenterY=-60.1 CenterZ=0 NormalX=0 NormalY=0 NormalZ=1 AngleXU=0 Radius=1.5
    g1: Circle CenterX=-15 CenterY=-60.1 CenterZ=0 NormalX=0 NormalY=0 NormalZ=1 AngleXU=0 Radius=1.5
  constraints (5):
    c: Equal(g0,g1)
    c: Diameter(g1) = 3
    c: DistanceX(g1,g0) = 30
    c: DistanceY(g1,g-1) = 60.1
    c: Symmetric(g1,g0,g-2)
FEATURE [Sketcher::SketchObject] Sketch023  label="screwHoleTop001"
  AttachmentOffset = pos=(0,0,19.8) rot=(0,0,1;0rad)
  ExternalGeometry = -> [Hole001]
  FullyConstrained = true
  MapMode = 5
  Placement = pos=(0,0,19.8) rot=(0,0,1;0rad)
  Support = -> [XY_Plane003]
  sketch-geometry (1):
    g0: Circle CenterX=-15 CenterY=0 CenterZ=0 NormalX=0 NormalY=0 NormalZ=1 AngleXU=0 Radius=1.5
  constraints (3):
    c: PointOnObject(g0,g-1)
    c: Diameter(g0) = 3
    c: Distance(g0,g-3) = 5
FEATURE [PartDesign::Hole] Hole003  label="screwHoleTop"
  BaseFeature = -> Hole001
  CustomThreadClearance = 0
  Depth = 25
  DepthType = 0
  Diameter = 3
  DrillForDepth = false
  DrillPoint = 1
  DrillPointAngle = 118
  HoleCutCountersinkAngle = 130
  HoleCutCustomValues = false
  HoleCutDepth = 0
  HoleCutDiameter = 6.1
  HoleCutType = 2
  ModelThread = false
  Profile = -> Sketch023
  Tapered = false
  TaperedAngle = 90
  ThreadClass = 0
  ThreadDepth = 25
  ThreadDepthType = 0
  ThreadDirection = 0
  ThreadFit = 0
  ThreadSize = 0
  ThreadType = 0
  Threaded = false
  UseCustomThreadClearance = false
FEATURE [PartDesign::Body] Body003  label="cameraBox002"
  Group = -> [Sketch009,Pad003,Thickness,Sketch010,Pocket004,Sketch011,SubtractivePipe,Boolean002,Sketch021,Hole001,Sketch023,Hole003]
  Origin = -> Origin003
  Placement = pos=(0.0466892,-80.0429,0.0174524) rot=(0,0,-1;1.5708rad)
  Tip = -> Hole003
FEATURE [Sketcher::SketchObject] Sketch024  label="cameraTopScrewHole"
  AttachmentOffset = pos=(0,-4.7,18) rot=(0,0,1;0rad)
  FullyConstrained = true
  MapMode = 5
  Placement = pos=(0,-4.7,18) rot=(0,0,1;0rad)
  Support = -> [XY_Plane008]
  sketch-geometry (1):
    g0: Circle CenterX=0 CenterY=-60.3 CenterZ=0 NormalX=0 NormalY=0 NormalZ=1 AngleXU=0 Radius=1.5
  constraints (3):
    c: PointOnObject(g0,g-2)
    c: Diameter(g0) = 3
    c: DistanceY(g0,g-1) = 60.3
FEATURE [Part::Part2DObjectPython] Clone2D  label="verticalPipe (2D)"  # Draft 2D object (typed FeaturePython)
  Fuse = false
  Objects = -> [Sketch018]
  Placement = pos=(0,0,145) rot=(0,0,1;0rad)
  Scale = (1,1,1)
  expr: .Placement.Base.z = <<Parameter>>.verticalHeight
FEATURE [Part::Part2DObjectPython] Clone2D001  label="horizontalPipe (2D)"  # Draft 2D object (typed FeaturePython)
  Fuse = false
  Objects = -> [Sketch015]
  Placement = pos=(0,-69.5,0) rot=(1,0,0;1.5708rad)
  Scale = (1,1,1)
  expr: .Placement.Base.y = -<<Parameter>>.horizontalDepth
FEATURE [PartDesign::AdditiveLoft] AdditiveLoft  label="topSevoPipe"
  Closed = false
  Placement = pos=(0,0,145) rot=(0,0,1;0rad)
  Profile = -> Clone2D
  Ruled = false
  Sections = -> [Sketch018]
FEATURE [PartDesign::AdditivePipe] AdditivePipe  label="middelPipe"
  AuxilleryCurvelinear = true
  AuxillerySpineTangent = false
  BaseFeature = -> AdditiveLoft
  Binormal = (0,0,0)
  Mode = 0
  Placement = pos=(0,0,145) rot=(0,0,1;0rad)
  Profile = -> Sketch018
  Sections = -> [Sketch015]
  Spine = -> Sketch017
  SpineTangent = false
  Transformation = 1
  Transition = 0
FEATURE [PartDesign::AdditiveLoft] AdditiveLoft001  label="horizontalCameraPipe"
  BaseFeature = -> AdditivePipe
  Closed = false
  Placement = pos=(0,0,145) rot=(0,0,1;0rad)
  Profile = -> Sketch015
  Ruled = false
  Sections = -> [Clone2D001]
FEATURE [PartDesign::Pocket] Pocket  label="servoCutout"
  BaseFeature = -> AdditiveLoft001
  Direction = (0,1,2e-16)
  Length = 5
  Length2 = 5
  Midplane = true
  Placement = pos=(0,0,145) rot=(0,0,1;0rad)
  Profile = -> Sketch
  ReferenceAxis = -> Sketch [N_Axis]
  Type = 1
FEATURE [PartDesign::Hole] Hole  label="servoScrewHole001"
  BaseFeature = -> Pocket
  CustomThreadClearance = 0
  Depth = 397.15
  DepthType = 1
  Diameter = 2.7
  DrillForDepth = false
  DrillPoint = 1
  DrillPointAngle = 118
  HoleCutCountersinkAngle = 90
  HoleCutCustomValues = false
  HoleCutDepth = 0
  HoleCutDiameter = 6.1
  HoleCutType = 0
  ModelThread = false
  Placement = pos=(0,0,145) rot=(0,0,1;0rad)
  Profile = -> Sketch019
  Tapered = false
  TaperedAngle = 90
  ThreadClass = 0
  ThreadDepth = 397.15
  ThreadDepthType = 0
  ThreadDirection = 0
  ThreadFit = 0
  ThreadSize = 0
  ThreadType = 0
  Threaded = false
  UseCustomThreadClearance = false
  expr: Diameter = <<Parameter>>.servoScewHoleDiameter
FEATURE [PartDesign::Pocket] Pocket005  label="cableRoute001"
  BaseFeature = -> Hole
  Direction = (0,1,2e-16)
  Length = 5
  Length2 = 5
  Placement = pos=(0,0,145) rot=(0,0,1;0rad)
  Profile = -> Sketch020
  ReferenceAxis = -> Sketch020 [N_Axis]
  Type = 1
FEATURE [PartDesign::Hole] Hole004  label="cameraBottomScrewHole"
  BaseFeature = -> Pocket005
  CustomThreadClearance = 0
  Depth = 25
  DepthType = 0
  Diameter = 3
  DrillForDepth = false
  DrillPoint = 1
  DrillPointAngle = 118
  HoleCutCountersinkAngle = 90
  HoleCutCustomValues = false
  HoleCutDepth = 0
  HoleCutDiameter = 6.1
  HoleCutType = 0
  ModelThread = false
  Placement = pos=(0,0,145) rot=(0,0,1;0rad)
  Profile = -> Sketch022
  Reversed = true
  Tapered = false
  TaperedAngle = 90
  ThreadClass = 0
  ThreadDepth = 25
  ThreadDepthType = 0
  ThreadDirection = 0
  ThreadFit = 0
  ThreadSize = 0
  ThreadType = 0
  Threaded = false
  UseCustomThreadClearance = false
FEATURE [PartDesign::Hole] Hole005  label="cameraTopScrewHole001"
  BaseFeature = -> Hole004
  CustomThreadClearance = 0
  Depth = 25
  DepthType = 0
  Diameter = 3
  DrillForDepth = false
  DrillPoint = 1
  DrillPointAngle = 118
  HoleCutCountersinkAngle = 90
  HoleCutCustomValues = false
  HoleCutDepth = 0
  HoleCutDiameter = 6.1
  HoleCutType = 0
  ModelThread = false
  Placement = pos=(0,0,145) rot=(0,0,1;0rad)
  Profile = -> Sketch024
  Tapered = false
  TaperedAngle = 90
  ThreadClass = 0
  ThreadDepth = 25
  ThreadDepthType = 0
  ThreadDirection = 0
  ThreadFit = 0
  ThreadSize = 0
  ThreadType = 0
  Threaded = false
  UseCustomThreadClearance = false
FEATURE [PartDesign::Body] Body008  label="Unit"
  Group = -> [Sketch015,Sketch018,Sketch,Sketch019,Sketch020,Sketch022,Sketch024,Clone2D001,Clone2D,Sketch017,AdditiveLoft,AdditivePipe,AdditiveLoft001,Pocket,Hole,Pocket005,Hole004,Hole005]
  Origin = -> Origin008
  Tip = -> Hole005
